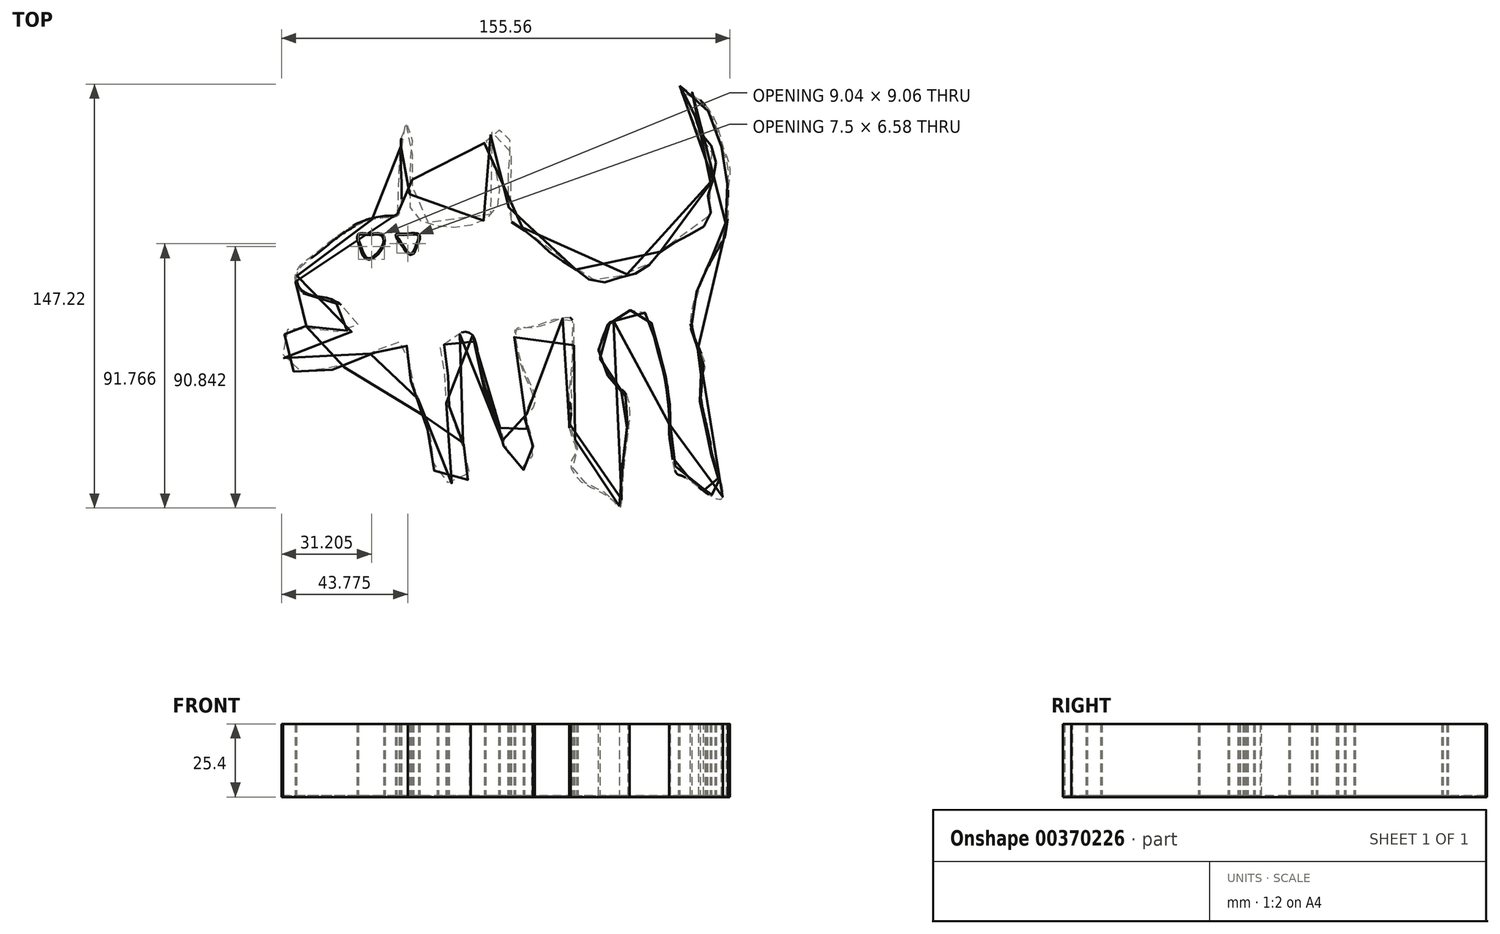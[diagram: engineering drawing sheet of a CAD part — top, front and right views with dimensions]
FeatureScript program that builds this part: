
annotation { "Feature Type Name" : "Feature", "Feature Type Description" : "" }
export const myFeature = defineFeature(function(context is Context, id is Id, definition is map)
    precondition{}
    {
        {
            var Q0;
            Q0=qCreatedBy(makeId("Top.planeOp"),FACE);
            var sketch = newSketch(context, id + "F0", { "sketchPlane" : qUnion([Q0])});
            skPoint(sketch, "E0.17.internal.orphan", {"position": v(0, 42.96) * mm});
            skPoint(sketch, "E1.23.internal.orphan", {"position": v(0, 13.15) * mm});
            skPoint(sketch, "E1.42.internal.orphan", {"position": v(39.47, 0) * mm});
            skPoint(sketch, "E1.58.internal.orphan", {"position": v(0, -16.65) * mm});
            skFitSpline(sketch, "E2", {"points": [v(-46.99, 29.26) * mm, v(-46.45, 48.6) * mm, v(-44.57, 60.68) * mm, v(-41.62, 56.92) * mm, v(-42.42, 46.18) * mm, v(-41.88, 39.73) * mm, v(-40.54, 28.46) * mm, v(-14.77, 29) * mm, v(-14.5, 46.71) * mm, v(-16.38, 55.3) * mm, v(-9.13, 58.53) * mm, v(-8.32, 40.27) * mm, v(-7.79, 32.48) * mm, v(-8.32, 27.92) * mm, v(-7.79, 27.11) * mm, v(0, 21.74) * mm, v(7.25, 15.3) * mm, v(15.84, 9.66) * mm, v(18.53, 7.25) * mm, v(25.78, 5.9) * mm, v(30.07, 7.51) * mm, v(35.98, 9.13) * mm, v(41.35, 13.15) * mm, v(44.84, 17.18) * mm, v(61.22, 27.38) * mm, v(60.14, 31.95) * mm, v(62.02, 41.34) * mm, v(63.1, 45.64) * mm, v(59.6, 55.57) * mm, v(57.19, 57.45) * mm, v(55.58, 63.36) * mm, v(50.48, 74.1) * mm, v(61.22, 64.97) * mm, v(65.51, 53.7) * mm, v(68.2, 45.1) * mm, v(67.66, 37.59) * mm, v(67.66, 30.07) * mm, v(66.59, 21.48) * mm, v(65.51, 19.06) * mm, v(60.41, 9.93) * mm, v(56.65, 0) * mm, v(55.04, -8.06) * mm, v(56.92, -16.11) * mm, v(59.6, -23.63) * mm, v(58, -29.8) * mm, v(61.22, -48.87) * mm, v(62.56, -55.31) * mm, v(65.51, -69.81) * mm, v(57.73, -66.05) * mm, v(51.28, -61.76) * mm, v(49.94, -61.22) * mm, v(48.6, -57.2) * mm, v(48.06, -53.16) * mm, v(47.25, -48.06) * mm, v(47.25, -42.7) * mm, v(46.99, -37.6) * mm, v(45.37, -26.58) * mm, v(42.42, -15.3) * mm, v(37.05, -4.84) * mm, v(23.9, -13.43) * mm, v(27.92, -29) * mm, v(33.02, -35.17) * mm, v(31.41, -59.07) * mm, v(30.07, -73.03) * mm, v(27.12, -69.81) * mm, v(16.65, -63.9) * mm, v(13.16, -57.2) * mm, v(15.04, -53.43) * mm, v(12.62, -45.38) * mm, v(13.16, -40.54) * mm, v(12.62, -35.98) * mm, v(12.89, -29) * mm, v(13.7, -20.4) * mm, v(13.7, -12.9) * mm, v(12.89, -6.98) * mm, v(0, -10.47) * mm, v(-5.64, -10.74) * mm, v(-3.76, -23.63) * mm, v(0, -32.22) * mm, v(0, -38.13) * mm, v(-2.95, -41.89) * mm, v(0, -48.06) * mm, v(0, -51.28) * mm, v(0, -59.07) * mm, v(-2.95, -59.88) * mm, v(-6.98, -57.46) * mm, v(-10.2, -51.55) * mm, v(-11.28, -47.53) * mm, v(-12.08, -44.84) * mm, v(-12.89, -40.81) * mm, v(-15.57, -35.44) * mm, v(-19.33, -22.02) * mm, v(-22.28, -12.62) * mm, v(-29.8, -15.3) * mm, v(-32.76, -20.95) * mm, v(-29.27, -27.93) * mm, v(-29.8, -34.64) * mm, v(-29, -38.13) * mm, v(-24.97, -48.33) * mm, v(-22.82, -55.31) * mm, v(-22.28, -62.83) * mm, v(-30.6, -64.44) * mm, v(-35.17, -56.92) * mm, v(-36.25, -47.26) * mm, v(-41.35, -32.5) * mm, v(-43.5, -21.75) * mm, v(-43.76, -16.92) * mm, v(-45.1, -15.84) * mm, v(-53.16, -18.26) * mm, v(-66.32, -24.44) * mm, v(-73.3, -25.24) * mm, v(-82.7, -25.78) * mm, v(-87.26, -19.33) * mm, v(-85.11, -9.67) * mm, v(-84.3, -8.86) * mm, v(-78.94, -9.94) * mm, v(-73.57, -10.47) * mm, v(-61.22, -10.47) * mm, v(-68.46, -1.88) * mm, v(-74.9, 0) * mm, v(-81.08, 2.68) * mm, v(-82.16, 9.13) * mm, v(-77.06, 14.23) * mm, v(-67.66, 21.74) * mm, v(-57.73, 27.11) * mm, v(-49.94, 28.46) * mm, v(-46.99, 29.26) * mm]});
            skFitSpline(sketch, "E3", {"points": [v(-59.87, 18.25) * mm, v(-57.19, 13.7) * mm, v(-52.09, 18.8) * mm, v(-52.9, 21.74) * mm, v(-56.65, 21.74) * mm, v(-60.41, 21.74) * mm, v(-59.87, 18.25) * mm]});
            skFitSpline(sketch, "E4", {"points": [v(-47.25, 21.74) * mm, v(-45.1, 21.74) * mm, v(-40, 21.74) * mm, v(-40.54, 18.52) * mm, v(-42.42, 15.3) * mm, v(-45.1, 18.25) * mm, v(-47.25, 21.74) * mm]});
            skSolve(sketch);
        }
        {
            var Q0;
            Q0=makeQuery(id+"F0.imprint","IMPRINT",FACE,{"disambiguationData":[TD([[makeQuery(id+"F0.imprint","IMPRINT",EDGE,{"derivedFrom":sQuery(id+"F0.wireOp",EDGE,"E2")}),-1.0]])]});
            extrude(context, id + "F1", {"entities" : qUnion([Q0]), "depth" : 25.4 * mm});
        }
        {
            var Q0;
            Q0=makeQuery(id+"F1.opExtrude","CAP_FACE",FACE,{"disambiguationData":[OSD([sQuery(id+"F0.wireOp",EDGE,"E2"),sQuery(id+"F0.wireOp",EDGE,"E3"),sQuery(id+"F0.wireOp",EDGE,"E4")])],"isStart":false});
            shell(context, id + "F2", {"entities" : qUnion([Q0]), "thickness" : 0.5 * mm});
        }
    });
